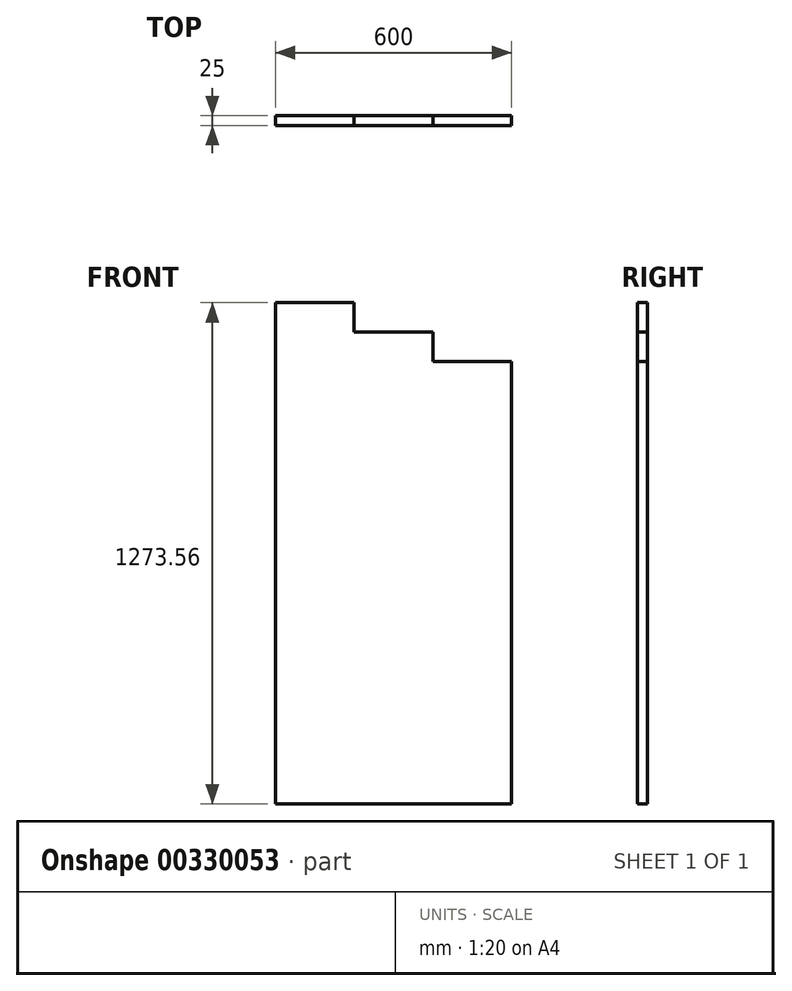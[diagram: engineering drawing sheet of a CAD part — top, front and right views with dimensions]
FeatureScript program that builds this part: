
annotation { "Feature Type Name" : "Feature", "Feature Type Description" : "" }
export const myFeature = defineFeature(function(context is Context, id is Id, definition is map)
    precondition{}
    {
        {
            var Q0;
            Q0=qCreatedBy(makeId("Front.planeOp"),FACE);
            var sketch = newSketch(context, id + "F0", { "sketchPlane" : qUnion([Q0])});
            skLineSegment(sketch, "E0", {"start": v(-303.23, 665.93) * mm, "end": v(-303.23, -607.63) * mm});
            skLineSegment(sketch, "E1", {"start": v(-303.23, -607.63) * mm, "end": v(296.77, -607.63) * mm});
            skLineSegment(sketch, "E2", {"start": v(296.77, -607.63) * mm, "end": v(296.77, 515.93) * mm});
            skLineSegment(sketch, "E3", {"start": v(296.77, 515.93) * mm, "end": v(96.77, 515.93) * mm});
            skLineSegment(sketch, "E4", {"start": v(96.77, 515.93) * mm, "end": v(96.77, 590.93) * mm});
            skLineSegment(sketch, "E5", {"start": v(96.77, 590.93) * mm, "end": v(-103.23, 590.93) * mm});
            skLineSegment(sketch, "E6", {"start": v(-103.23, 590.93) * mm, "end": v(-103.23, 665.93) * mm});
            skLineSegment(sketch, "E7", {"start": v(-103.23, 665.93) * mm, "end": v(-303.23, 665.93) * mm});
            skSolve(sketch);
        }
        {
            var Q0;
            Q0=makeQuery(id+"F0.imprint","IMPRINT",FACE,{"disambiguationData":[TD([[makeQuery(id+"F0.imprint","IMPRINT",EDGE,{"derivedFrom":sQuery(id+"F0.wireOp",EDGE,"E0")}),1.0]])]});
            extrude(context, id + "F1", {"entities" : qUnion([Q0]), "depth" : 25 * mm});
        }
    });
